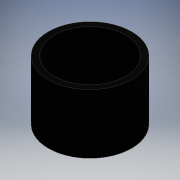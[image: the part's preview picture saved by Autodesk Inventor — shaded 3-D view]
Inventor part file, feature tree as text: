
AUTODESK INVENTOR PART (.ipt)
format: ipt  version: 2016 (Build 200138000, 138)  size: 90,112 bytes
history: native  units: mm
features: other x1, extrude x1, sketch x1
ambient origin geometry x8: Origin, YZ Plane, XZ Plane, XY Plane, X Axis, Y Axis, Z Axis, Center Point
bodies: Body1 (feature_tree)
feature tree (3):
  other  "ソリッド1"
  extrude  "押し出し1"  Depth=14.0mm
  sketch  "スケッチ1"
